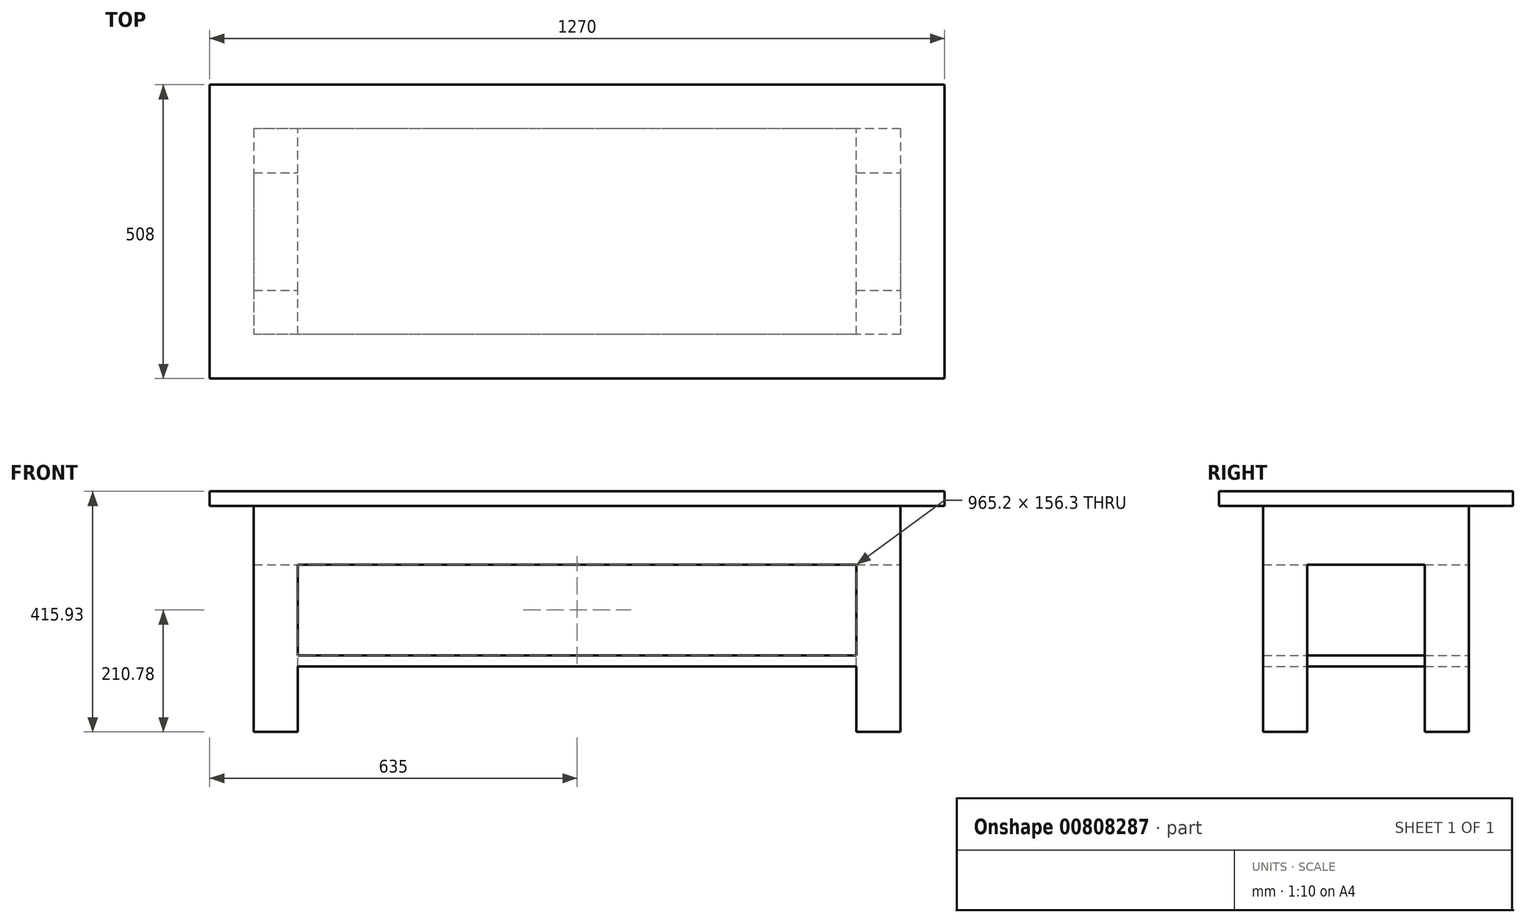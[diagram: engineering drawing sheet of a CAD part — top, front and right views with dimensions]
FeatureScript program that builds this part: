
annotation { "Feature Type Name" : "Feature", "Feature Type Description" : "" }
export const myFeature = defineFeature(function(context is Context, id is Id, definition is map)
    precondition{}
    {
        {
            var Q0;
            Q0=qCreatedBy(makeId("Top.planeOp"),FACE);
            var sketch = newSketch(context, id + "F0", { "sketchPlane" : qUnion([Q0])});
            skLineSegment(sketch, "E0.bottom", {"start": v(635, -254) * mm, "end": v(-635, -254) * mm});
            skLineSegment(sketch, "E0.top", {"start": v(635, 254) * mm, "end": v(-635, 254) * mm});
            skLineSegment(sketch, "E0.left", {"start": v(635, -254) * mm, "end": v(635, 254) * mm});
            skLineSegment(sketch, "E0.right", {"start": v(-635, -254) * mm, "end": v(-635, 254) * mm});
            skPoint(sketch, "E0.middle", {"position": v(0, 0) * mm});
            skSolve(sketch);
        }
        {
            var Q0;
            Q0 = qSketchRegion(id + "F0", true);
            extrude(context, id + "F1", {"entities" : qUnion([Q0]), "depth" : 25.4 * mm, "offsetDistance" : 25.4 * mm});
        }
        {
            var Q0;
            Q0=makeQuery(id+"F1.opExtrude","CAP_FACE",FACE,{"disambiguationData":[OSD([sQuery(id+"F0.wireOp",EDGE,"E0.bottom"),sQuery(id+"F0.wireOp",EDGE,"E0.top"),sQuery(id+"F0.wireOp",EDGE,"E0.left"),sQuery(id+"F0.wireOp",EDGE,"E0.right")])],"isStart":true});
            var sketch = newSketch(context, id + "F2", { "sketchPlane" : qUnion([Q0])});
            skLineSegment(sketch, "E1.bottom", {"start": v(558.8, -177.8) * mm, "end": v(-558.8, -177.8) * mm});
            skLineSegment(sketch, "E1.top", {"start": v(558.8, 177.8) * mm, "end": v(-558.8, 177.8) * mm});
            skLineSegment(sketch, "E1.left", {"start": v(558.8, -177.8) * mm, "end": v(558.8, 177.8) * mm});
            skLineSegment(sketch, "E1.right", {"start": v(-558.8, -177.8) * mm, "end": v(-558.8, 177.8) * mm});
            skPoint(sketch, "E1.middle", {"position": v(0, 0) * mm});
            skSolve(sketch);
        }
        {
            var Q0;
            Q0 = qSketchRegion(id + "F2", true);
            extrude(context, id + "F3", {"entities" : qUnion([Q0]), "operationType" : NewBodyOperationType.ADD, "depth" : 101.6 * mm, "offsetDistance" : 25.4 * mm});
        }
        {
            var Q0;
            Q0=makeQuery(id+"F3.opExtrude","CAP_FACE",FACE,{"disambiguationData":[OSD([sQuery(id+"F2.wireOp",EDGE,"E1.bottom"),sQuery(id+"F2.wireOp",EDGE,"E1.top"),sQuery(id+"F2.wireOp",EDGE,"E1.left"),sQuery(id+"F2.wireOp",EDGE,"E1.right")])],"isStart":false});
            var sketch = newSketch(context, id + "F4", { "sketchPlane" : qUnion([Q0])});
            skLineSegment(sketch, "E2.bottom", {"start": v(-558.8, 177.8) * mm, "end": v(-482.6, 177.8) * mm});
            skLineSegment(sketch, "E2.top", {"start": v(-558.8, 101.6) * mm, "end": v(-482.6, 101.6) * mm});
            skLineSegment(sketch, "E2.left", {"start": v(-558.8, 177.8) * mm, "end": v(-558.8, 101.6) * mm});
            skLineSegment(sketch, "E2.right", {"start": v(-482.6, 177.8) * mm, "end": v(-482.6, 101.6) * mm});
            skLineSegment(sketch, "E3.0.1.0", {"start": v(-558.8, -101.6) * mm, "end": v(-482.6, -101.6) * mm});
            skLineSegment(sketch, "E3.0.1.1", {"start": v(-558.8, -101.6) * mm, "end": v(-558.8, -177.8) * mm});
            skLineSegment(sketch, "E3.0.1.2", {"start": v(-482.6, -101.6) * mm, "end": v(-482.6, -177.8) * mm});
            skLineSegment(sketch, "E3.0.1.3", {"start": v(-558.8, -177.8) * mm, "end": v(-482.6, -177.8) * mm});
            skLineSegment(sketch, "E3.1.0.0", {"start": v(482.6, 177.8) * mm, "end": v(558.8, 177.8) * mm});
            skLineSegment(sketch, "E3.1.0.1", {"start": v(482.6, 177.8) * mm, "end": v(482.6, 101.6) * mm});
            skLineSegment(sketch, "E3.1.0.2", {"start": v(558.8, 177.8) * mm, "end": v(558.8, 101.6) * mm});
            skLineSegment(sketch, "E3.1.0.3", {"start": v(482.6, 101.6) * mm, "end": v(558.8, 101.6) * mm});
            skLineSegment(sketch, "E3.1.1.0", {"start": v(482.6, -101.6) * mm, "end": v(558.8, -101.6) * mm});
            skLineSegment(sketch, "E3.1.1.1", {"start": v(482.6, -101.6) * mm, "end": v(482.6, -177.8) * mm});
            skLineSegment(sketch, "E3.1.1.2", {"start": v(558.8, -101.6) * mm, "end": v(558.8, -177.8) * mm});
            skLineSegment(sketch, "E3.1.1.3", {"start": v(482.6, -177.8) * mm, "end": v(558.8, -177.8) * mm});
            skLineSegment(sketch, "E3.direction1", {"start": v(-558.8, 101.6) * mm, "end": v(482.6, 101.6) * mm, "construction": true});
            skLineSegment(sketch, "E3.direction2", {"start": v(-558.8, 101.6) * mm, "end": v(-558.8, -177.8) * mm, "construction": true});
            skSolve(sketch);
        }
        {
            var Q0;
            Q0 = qSketchRegion(id + "F4", true);
            extrude(context, id + "F5", {"entities" : qUnion([Q0]), "operationType" : NewBodyOperationType.ADD, "depth" : 288.93 * mm, "offsetDistance" : 25.4 * mm});
        }
        {
            var Q0;
            Q0=makeQuery(id+"F5.opExtrude","SWEPT_FACE",FACE,{"disambiguationData":[OSD([sQuery(id+"F4.wireOp",EDGE,"E2.right")])]});
            var sketch = newSketch(context, id + "F6", { "sketchPlane" : qUnion([Q0])});
            skLineSegment(sketch, "E4.bottom", {"start": v(-177.8, -257.9) * mm, "end": v(177.8, -257.9) * mm});
            skLineSegment(sketch, "E4.top", {"start": v(-177.8, -276.95) * mm, "end": v(177.8, -276.95) * mm});
            skLineSegment(sketch, "E4.left", {"start": v(-177.8, -257.9) * mm, "end": v(-177.8, -276.95) * mm});
            skLineSegment(sketch, "E4.right", {"start": v(177.8, -257.9) * mm, "end": v(177.8, -276.95) * mm});
            skLineSegment(sketch, "E5.0", {"start": v(177.8, -390.53) * mm, "end": v(177.8, -101.6) * mm, "construction": true});
            skSolve(sketch);
        }
        {
            var Q0;
            Q0 = qSketchRegion(id + "F6", true);
            var Q1;
            Q1=makeQuery(id+"F5.opExtrude","SWEPT_FACE",FACE,{"disambiguationData":[OSD([sQuery(id+"F4.wireOp",EDGE,"E3.1.0.1")])]});
            extrude(context, id + "F7", {"entities" : qUnion([Q0]), "operationType" : NewBodyOperationType.ADD, "endBound" : BoundingType.UP_TO_SURFACE, "depth" : 25.4 * mm, "endBoundEntityFace" : qUnion([Q1]), "offsetDistance" : 25.4 * mm});
        }
    });
